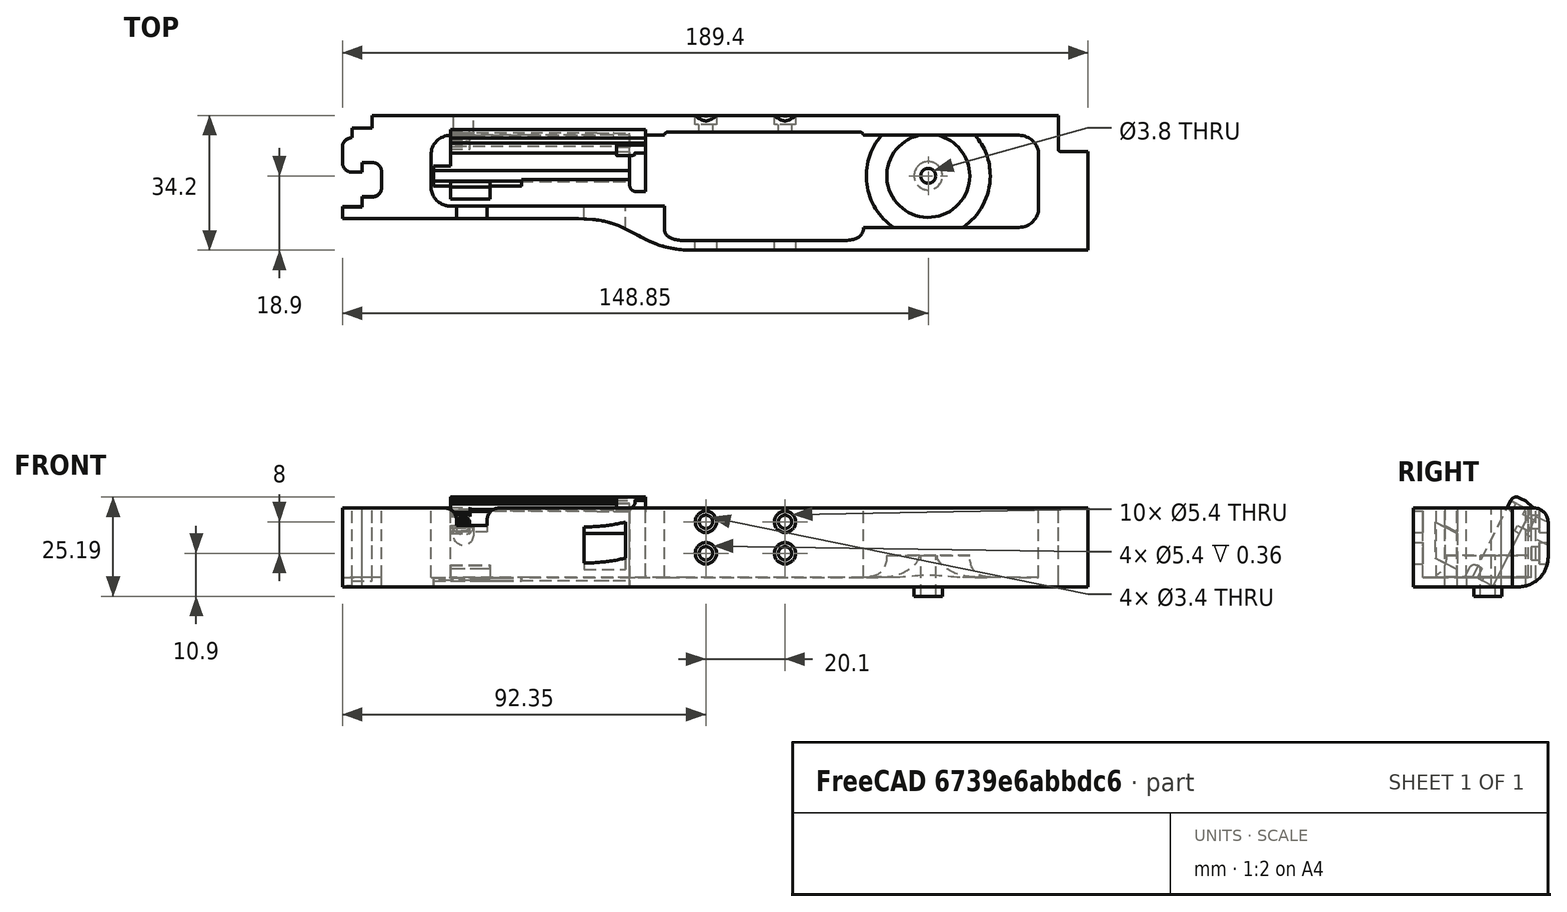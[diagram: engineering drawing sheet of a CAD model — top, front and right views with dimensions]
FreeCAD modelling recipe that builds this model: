
FCSTD DOCUMENT  (FreeCAD 0.19R0.19.2)
Label: v0_993
License: All rights reserved
LicenseURL: http://en.wikipedia.org/wiki/All_rights_reserved
objects: Sketcher::SketchObject×37, Part::Extrusion×31, Part::Cut×14, Part::Fillet×13, Part::MultiFuse×12, Part::Box×8, App::MeasureDistance×4, Part::Revolution×1, Mesh::Feature×1
note: 116 computed .brp shape members not serialized (recipe doc carries the construction recipe); baked Part::Feature solids carry a one-line shape summary decoded from their .brp

FEATURE [Sketcher::SketchObject] Sketch
  FullyConstrained = true
  sketch-geometry (36):
    g0: LineSegment StartX=0 StartY=0 StartZ=0 EndX=154.4 EndY=0 EndZ=0
    g1: LineSegment StartX=154.4 StartY=0 StartZ=0 EndX=154.4 EndY=-7.6 EndZ=0
    g2: LineSegment StartX=32.5209 StartY=-26.2 StartZ=0 EndX=-7.5 EndY=-26.2 EndZ=0
    g3-g7: Circle x5 (B-spline internal-alignment scaffolding for g8; pole/knot coordinates omitted)
    g8: BSplineCurve PolesCount=5 KnotsCount=3 Degree=3 IsPeriodic=0
    g9: GeomPoint X=61.85 Y=-33.8 Z=0
    g10: GeomPoint X=47.185 Y=-29.9 Z=0
    g11: GeomPoint X=32.5209 Y=-26.2 Z=0
    g12: Circle CenterX=121.35 CenterY=-14.3 CenterZ=0 NormalX=0 NormalY=0 NormalZ=1 AngleXU=0 Radius=3.25
    g13: LineSegment StartX=-7.5 StartY=-26.2 StartZ=0 EndX=-27.5 EndY=-26.2 EndZ=0
    g14: LineSegment StartX=-20 StartY=0 StartZ=0 EndX=0 EndY=0 EndZ=0
    g15: LineSegment StartX=-25 StartY=-3.1 StartZ=0 EndX=-20 EndY=-3.1 EndZ=0
    g16: LineSegment StartX=-25 StartY=-3.1 StartZ=0 EndX=-25 EndY=-5.6 EndZ=0
    g17: LineSegment StartX=-27.5 StartY=-8.1 StartZ=0 EndX=-27.5 EndY=-11.85 EndZ=0
    g18: ArcOfCircle CenterX=-25 CenterY=-8.1 CenterZ=0 NormalX=0 NormalY=0 NormalZ=1 AngleXU=0 Radius=2.5 StartAngle=1.5708 EndAngle=3.14159
    g19: LineSegment StartX=-25 StartY=-14.35 StartZ=0 EndX=-22.5 EndY=-14.35 EndZ=0
    g20: ArcOfCircle CenterX=-25 CenterY=-11.85 CenterZ=0 NormalX=0 NormalY=0 NormalZ=1 AngleXU=0 Radius=2.5 StartAngle=3.14159 EndAngle=4.71239
    g21: LineSegment StartX=-22.5 StartY=-14.35 StartZ=0 EndX=-22.5 EndY=-11.85 EndZ=0
    g22: LineSegment StartX=-22.5 StartY=-11.85 StartZ=0 EndX=-20 EndY=-11.85 EndZ=0
    g23: ArcOfCircle CenterX=-20 CenterY=-14.35 CenterZ=0 NormalX=0 NormalY=0 NormalZ=1 AngleXU=0 Radius=2.5 StartAngle=8e-16 EndAngle=1.5708
    g24: LineSegment StartX=-17.5 StartY=-14.35 StartZ=0 EndX=-17.5 EndY=-18.1 EndZ=0
    g25: ArcOfCircle CenterX=-20 CenterY=-18.1 CenterZ=0 NormalX=0 NormalY=0 NormalZ=1 AngleXU=0 Radius=2.5 StartAngle=4.71239 EndAngle=6.28319
    g26: LineSegment StartX=-22.5 StartY=-20.6 StartZ=0 EndX=-20 EndY=-20.6 EndZ=0
    g27: LineSegment StartX=-22.5 StartY=-20.6 StartZ=0 EndX=-22.5 EndY=-23.1 EndZ=0
    g28: LineSegment StartX=-27.5 StartY=-23.1 StartZ=0 EndX=-22.5 EndY=-23.1 EndZ=0
    g29: LineSegment StartX=-20 StartY=-3.1 StartZ=0 EndX=-20 EndY=0 EndZ=0
    g30: LineSegment StartX=-27.5 StartY=-23.1 StartZ=0 EndX=-27.5 EndY=-26.2 EndZ=0
    g31: LineSegment StartX=154.4 StartY=-7.6 StartZ=0 EndX=154.4 EndY=-8.6 EndZ=0
    g32: ArcOfCircle CenterX=154.9 CenterY=-8.6 CenterZ=0 NormalX=0 NormalY=0 NormalZ=1 AngleXU=0 Radius=0.5 StartAngle=3.14159 EndAngle=4.71239
    g33: LineSegment StartX=154.9 StartY=-9.1 StartZ=0 EndX=161.9 EndY=-9.1 EndZ=0
    g34: LineSegment StartX=161.9 StartY=-9.1 StartZ=0 EndX=161.9 EndY=-33.8 EndZ=0
    g35: LineSegment StartX=161.9 StartY=-33.8 StartZ=0 EndX=61.85 EndY=-33.8 EndZ=0
  constraints (72):
    c: PointOnObject(g0,g-2)
    c: Horizontal(g0)
    c: Distance(g0) = 154.4
    c: DistanceY(g-1,g0) = 0
    c: Vertical(g1)
    c: Distance(g1) = 7.6
    c: Coincident(g1,g0)
    c: Horizontal(g2)
    c: Block(g2)
    c: Weight(g3) = 1
    c: Coincident(g8,g2)
    c: InternalAlignment(g3-g7 -> g8) x5
    c: InternalAlignment(g9,g8)
    c: InternalAlignment(g10,g8)
    c: InternalAlignment(g11,g8)
    c: Block(g12)
    c: Coincident(g13,g2)
    c: Horizontal(g13)
    c: Distance(g13) = 20
    c: Horizontal(g14)
    c: Distance(g14) = 20
    c: Coincident(g14,g0)
    c: Horizontal(g15)
    c: Vertical(g16)
    c: Coincident(g16,g15)
    c: Vertical(g17)
    c: Coincident(g18,g16)
    c: Block(g18)
    c: Coincident(g17,g18)
    c: Horizontal(g19)
    c: Coincident(g20,g17)
    c: Block(g20)
    c: Block(g19)
    c: Vertical(g21)
    c: Coincident(g21,g19)
    c: Horizontal(g22)
    c: Coincident(g22,g21)
    c: Coincident(g23,g22)
    c: Vertical(g24)
    c: Block(g23)
    c: Coincident(g24,g23)
    c: Coincident(g25,g24)
    c: Block(g25)
    c: Horizontal(g26)
    c: Coincident(g26,g25)
    c: Vertical(g27)
    c: Coincident(g27,g26)
    c: Horizontal(g28)
    c: Coincident(g28,g27)
    c: Block(g15)
    c: Block(g28)
    c: Coincident(g29,g15)
    c: Coincident(g29,g14)
    c: Vertical(g29)
    c: Coincident(g30,g28)
    c: Coincident(g30,g13)
    c: Vertical(g30)
    c: Vertical(g31)
    c: Distance(g31) = 1
    c: Coincident(g31,g1)
    c: Coincident(g32,g31)
    c: Block(g32)
    c: Coincident(g33,g32)
    c: Horizontal(g33)
    c: Coincident(g34,g33)
    c: Vertical(g34)
    c: Block(g34)
    c: Coincident(g35,g34)
    c: Horizontal(g35)
    c: Block(g35)
    c: Coincident(g8,g35)
    c: Block(g8)
FEATURE [Part::Extrusion] Extrude  label="mainBodyBaseExtrude"
  Base = -> Sketch
  Dir = (0,0,1)
  DirMode = 2
  FaceMakerClass = Part::FaceMakerBullseye
  LengthFwd = 2.4
  LengthRev = 0
  Solid = true
  Symmetric = false
FEATURE [Sketcher::SketchObject] Sketch001
  FullyConstrained = true
  sketch-geometry (75):
    g0: ArcOfCircle CenterX=144.4 CenterY=-10 CenterZ=0 NormalX=0 NormalY=0 NormalZ=1 AngleXU=0 Radius=5 StartAngle=4.345e-13 EndAngle=1.5708
    g1: LineSegment StartX=32.5209 StartY=-26.2 StartZ=0 EndX=-7.49911 EndY=-26.2 EndZ=0
    g2: LineSegment StartX=0 StartY=0 StartZ=0 EndX=154.4 EndY=0 EndZ=0
    g3-g7: Circle x5 (B-spline internal-alignment scaffolding for g8; pole/knot coordinates omitted)
    g8: BSplineCurve PolesCount=5 KnotsCount=3 Degree=3 IsPeriodic=0
    g9: GeomPoint X=61.85 Y=-33.8 Z=0
    g10: GeomPoint X=47.1857 Y=-29.9 Z=0
    g11: GeomPoint X=32.5209 Y=-26.2 Z=0
    g12: LineSegment StartX=154.4 StartY=0 StartZ=0 EndX=154.4 EndY=-7.6 EndZ=0
    g13: LineSegment StartX=20 StartY=-5 StartZ=0 EndX=54.35 EndY=-5 EndZ=0
    g14: LineSegment StartX=104.85 StartY=-5 StartZ=0 EndX=144.4 EndY=-5 EndZ=0
    g15: LineSegment StartX=54.35 StartY=-23 StartZ=0 EndX=20 EndY=-23 EndZ=0
    g16: LineSegment StartX=-27.4991 StartY=-26.2 StartZ=0 EndX=-7.49911 EndY=-26.2 EndZ=0
    g17: LineSegment StartX=-20 StartY=0 StartZ=0 EndX=0 EndY=0 EndZ=0
    g18: LineSegment StartX=-27.4991 StartY=-23.2 StartZ=0 EndX=-22.5 EndY=-23.2 EndZ=0
    g19: LineSegment StartX=-22.5 StartY=-20.7 StartZ=0 EndX=-22.5 EndY=-23.2 EndZ=0
    g20: LineSegment StartX=-22.5 StartY=-20.7 StartZ=0 EndX=-20 EndY=-20.7 EndZ=0
    g21: ArcOfCircle CenterX=-20 CenterY=-18.2 CenterZ=0 NormalX=0 NormalY=0 NormalZ=1 AngleXU=0 Radius=2.5 StartAngle=4.71239 EndAngle=6.28319
    g22: LineSegment StartX=-17.5 StartY=-14.4 StartZ=0 EndX=-17.5 EndY=-18.2 EndZ=0
    g23: ArcOfCircle CenterX=-20 CenterY=-14.4 CenterZ=0 NormalX=0 NormalY=0 NormalZ=1 AngleXU=0 Radius=2.5 StartAngle=9e-16 EndAngle=1.5708
    g24: LineSegment StartX=-22.5 StartY=-11.9 StartZ=0 EndX=-20 EndY=-11.9 EndZ=0
    g25: LineSegment StartX=-22.5 StartY=-14.4 StartZ=0 EndX=-22.5 EndY=-11.9 EndZ=0
    g26: LineSegment StartX=-25 StartY=-14.4 StartZ=0 EndX=-22.5 EndY=-14.4 EndZ=0
    g27: ArcOfCircle CenterX=-25 CenterY=-11.9 CenterZ=0 NormalX=0 NormalY=0 NormalZ=1 AngleXU=0 Radius=2.5 StartAngle=3.14159 EndAngle=4.71239
    g28: LineSegment StartX=-27.5 StartY=-8.1 StartZ=0 EndX=-27.5 EndY=-11.9 EndZ=0
    g29: ArcOfCircle CenterX=-25 CenterY=-8.1 CenterZ=0 NormalX=0 NormalY=0 NormalZ=1 AngleXU=0 Radius=2.5 StartAngle=1.5708 EndAngle=3.14159
    g30: LineSegment StartX=-25 StartY=-3.1 StartZ=0 EndX=-25 EndY=-5.6 EndZ=0
    g31: LineSegment StartX=-20 StartY=-3.1 StartZ=0 EndX=-25 EndY=-3.1 EndZ=0
    g32: LineSegment StartX=-20 StartY=0 StartZ=0 EndX=-20 EndY=-3.1 EndZ=0
    g33: LineSegment StartX=-27.4991 StartY=-26.2 StartZ=0 EndX=-27.4991 EndY=-23.2 EndZ=0
    g34: LineSegment StartX=4.09e-14 StartY=-5 StartZ=0 EndX=20 EndY=-5 EndZ=0
    g35: ArcOfCircle CenterX=7.1e-15 CenterY=-18 CenterZ=0 NormalX=0 NormalY=0 NormalZ=1 AngleXU=0 Radius=5 StartAngle=3.14159 EndAngle=4.71239
    g36: ArcOfCircle CenterX=4.26e-14 CenterY=-10 CenterZ=0 NormalX=0 NormalY=0 NormalZ=1 AngleXU=0 Radius=5 StartAngle=1.5708 EndAngle=3.14159
    g37: LineSegment StartX=-5 StartY=-18 StartZ=0 EndX=-5 EndY=-10 EndZ=0
    g38: LineSegment StartX=6.2e-15 StartY=-23 StartZ=0 EndX=20 EndY=-23 EndZ=0
    g39: LineSegment StartX=154.4 StartY=-7.6 StartZ=0 EndX=154.4 EndY=-8.6 EndZ=0
    g40: LineSegment StartX=154.9 StartY=-9.1 StartZ=0 EndX=161.9 EndY=-9.1 EndZ=0
    g41: ArcOfCircle CenterX=154.9 CenterY=-8.6 CenterZ=0 NormalX=0 NormalY=0 NormalZ=1 AngleXU=0 Radius=0.5 StartAngle=3.14159 EndAngle=4.71299
    g42: LineSegment StartX=104.85 StartY=-28.3916 StartZ=0 EndX=144.408 EndY=-28.3916 EndZ=0
    g43: LineSegment StartX=149.4 StartY=-10 StartZ=0 EndX=149.4 EndY=-23.4 EndZ=0
    g44: ArcOfCircle CenterX=144.408 CenterY=-23.4 CenterZ=0 NormalX=0 NormalY=0 NormalZ=1 AngleXU=0 Radius=4.99164 StartAngle=4.71239 EndAngle=6.28319
    g45: LineSegment StartX=104.85 StartY=-28.3916 StartZ=0 EndX=104.85 EndY=-28.7833 EndZ=0
    g46: LineSegment StartX=54.35 StartY=-28.7916 StartZ=0 EndX=54.35 EndY=-23 EndZ=0
    g47: LineSegment StartX=161.9 StartY=-33.8 StartZ=0 EndX=161.9 EndY=-9.1 EndZ=0
    g48: LineSegment StartX=61.85 StartY=-33.8 StartZ=0 EndX=161.9 EndY=-33.8 EndZ=0
    g49: Circle CenterX=54.35 CenterY=-28.7916 CenterZ=0 NormalX=0 NormalY=0 NormalZ=1 AngleXU=0 Radius=1
    g50: Circle CenterX=54.35 CenterY=-31.7916 CenterZ=0 NormalX=0 NormalY=0 NormalZ=1 AngleXU=0 Radius=1
    g51: Circle CenterX=57.35 CenterY=-31.7916 CenterZ=0 NormalX=0 NormalY=0 NormalZ=1 AngleXU=0 Radius=1
    g52: BSplineCurve PolesCount=3 KnotsCount=2 Degree=2 IsPeriodic=0
    g53: GeomPoint X=54.35 Y=-28.7916 Z=0
    g54: GeomPoint X=57.35 Y=-31.7916 Z=0
    g55: Circle CenterX=104.85 CenterY=-28.7833 CenterZ=0 NormalX=0 NormalY=0 NormalZ=1 AngleXU=0 Radius=1
    g56: Circle CenterX=104.85 CenterY=-31.7916 CenterZ=0 NormalX=0 NormalY=0 NormalZ=1 AngleXU=0 Radius=1
    g57: Circle CenterX=101.85 CenterY=-31.7916 CenterZ=0 NormalX=0 NormalY=0 NormalZ=1 AngleXU=0 Radius=1
    g58: BSplineCurve PolesCount=3 KnotsCount=2 Degree=2 IsPeriodic=0
    g59: GeomPoint X=104.85 Y=-28.7833 Z=0
    g60: GeomPoint X=101.85 Y=-31.7916 Z=0
    g61: LineSegment StartX=57.35 StartY=-31.7916 StartZ=0 EndX=101.85 EndY=-31.7916 EndZ=0
    g62: Circle CenterX=54.35 CenterY=-5 CenterZ=0 NormalX=0 NormalY=0 NormalZ=1 AngleXU=0 Radius=1
    g63: Circle CenterX=54.35 CenterY=-4 CenterZ=0 NormalX=0 NormalY=0 NormalZ=1 AngleXU=0 Radius=1
    g64: Circle CenterX=55.15 CenterY=-4 CenterZ=0 NormalX=0 NormalY=0 NormalZ=1 AngleXU=0 Radius=1
    g65: BSplineCurve PolesCount=3 KnotsCount=2 Degree=2 IsPeriodic=0
    g66: GeomPoint X=54.35 Y=-5 Z=0
    g67: GeomPoint X=55.15 Y=-4 Z=0
    g68: Circle CenterX=104.85 CenterY=-5 CenterZ=0 NormalX=0 NormalY=0 NormalZ=1 AngleXU=0 Radius=1
    g69: Circle CenterX=104.85 CenterY=-4 CenterZ=0 NormalX=0 NormalY=0 NormalZ=1 AngleXU=0 Radius=1
    g70: Circle CenterX=104.05 CenterY=-4 CenterZ=0 NormalX=0 NormalY=0 NormalZ=1 AngleXU=0 Radius=1
    g71: BSplineCurve PolesCount=3 KnotsCount=2 Degree=2 IsPeriodic=0
    g72: GeomPoint X=104.85 Y=-5 Z=0
    g73: GeomPoint X=104.05 Y=-4 Z=0
    g74: LineSegment StartX=104.05 StartY=-4 StartZ=0 EndX=55.15 EndY=-4 EndZ=0
  constraints (156):
    c: PointOnObject(g2,g-2)
    c: DistanceY(g-1,g2) = 0
    c: Block(g0)
    c: Horizontal(g1)
    c: Distance(g1) = 40.02
    c: Horizontal(g2)
    c: Block(g2)
    c: Weight(g3) = 1
    c: Equal(g3, g4-g7) x4
    c: Coincident(g8,g1)
    c: InternalAlignment(g3-g7 -> g8) x5
    c: InternalAlignment(g9,g8)
    c: InternalAlignment(g10,g8)
    c: InternalAlignment(g11,g8)
    c: Vertical(g12)
    c: Coincident(g12,g2)
    c: Distance(g12) = 7.6
    c: Block(g12)
    c: Horizontal(g13)
    c: Coincident(g14,g0)
    c: Horizontal(g14)
    c: Horizontal(g15)
    c: Horizontal(g16)
    c: Distance(g16) = 20
    c: Coincident(g1,g16)
    c: Horizontal(g17)
    c: Distance(g17) = 20
    c: Coincident(g17,g2)
    c: Horizontal(g31)
    c: Vertical(g30)
    c: Coincident(g29,g30)
    c: Vertical(g28)
    c: Block(g29)
    c: Coincident(g27,g28)
    c: Block(g27)
    c: Horizontal(g26)
    c: Coincident(g26,g27)
    c: Vertical(g25)
    c: Coincident(g25,g26)
    c: Horizontal(g24)
    c: Coincident(g23,g24)
    c: Block(g23)
    c: Vertical(g22)
    c: Coincident(g21,g22)
    c: Block(g21)
    c: Horizontal(g20)
    c: Coincident(g20,g21)
    c: Vertical(g19)
    c: Coincident(g19,g20)
    c: Horizontal(g18)
    c: Coincident(g18,g19)
    c: Coincident(g32,g17)
    c: Coincident(g32,g31)
    c: Vertical(g32)
    c: Coincident(g33,g16)
    c: Coincident(g33,g18)
    c: Vertical(g33)
    c: Block(g33)
    c: Block(g18)
    c: Block(g22)
    c: Block(g26)
    c: Block(g25)
    c: Block(g24)
    c: Block(g28)
    c: Block(g31)
    c: Block(g30)
    c: Horizontal(g34)
    c: Distance(g34) = 20
    c: Block(g35)
    c: Block(g36)
    c: Coincident(g37,g35)
    c: Coincident(g37,g36)
    c: Vertical(g37)
    c: Coincident(g38,g35)
    c: Coincident(g38,g15)
    c: Horizontal(g38)
    c: Block(g38)
    c: Block(g34)
    c: Block(g13)
    c: Vertical(g39)
    c: Distance(g39) = 1
    c: Coincident(g39,g12)
    c: Horizontal(g40)
    c: Coincident(g41,g39)
    c: Coincident(g41,g40)
    c: Block(g39)
    c: Block(g41)
    c: Horizontal(g42)
    c: Vertical(g43)
    c: Distance(g43) = 13.4
    c: Coincident(g43,g0)
    c: Block(g42)
    c: Block(g43)
    c: Coincident(g44,g43)
    c: Coincident(g44,g42)
    c: Block(g44)
    c: Distance(g15) = 34.35
    c: Coincident(g45,g42)
    c: Vertical(g45)
    c: Coincident(g46,g15)
    c: Vertical(g46)
    c: Coincident(g47,g40)
    c: Vertical(g47)
    c: Block(g47)
    c: Coincident(g48,g47)
    c: Horizontal(g48)
    c: Block(g48)
    c: Coincident(g8,g48)
    c: Block(g8)
    c: Coincident(g52,g46)
    c: Weight(g49) = 1
    c: Equal(g49,g50)
    c: Equal(g49,g51)
    c: InternalAlignment(g49,g52)
    c: InternalAlignment(g50,g52)
    c: InternalAlignment(g51,g52)
    c: InternalAlignment(g53,g52)
    c: InternalAlignment(g54,g52)
    c: Coincident(g58,g45)
    c: Weight(g55) = 1
    c: Equal(g55,g56)
    c: Equal(g55,g57)
    c: InternalAlignment(g55,g58)
    c: InternalAlignment(g56,g58)
    c: InternalAlignment(g57,g58)
    c: InternalAlignment(g59,g58)
    c: InternalAlignment(g60,g58)
    c: Block(g58)
    c: Block(g52)
    c: Coincident(g61,g52)
    c: Coincident(g61,g58)
    c: Horizontal(g61)
    c: Block(g14)
    c: Coincident(g65,g13)
    c: Weight(g62) = 1
    c: Equal(g62,g63)
    c: Equal(g62,g64)
    c: InternalAlignment(g62,g65)
    c: InternalAlignment(g63,g65)
    c: InternalAlignment(g64,g65)
    c: InternalAlignment(g66,g65)
    c: InternalAlignment(g67,g65)
    c: Block(g65)
    c: Coincident(g71,g14)
    c: Weight(g68) = 1
    c: Equal(g68,g69)
    c: Equal(g68,g70)
    c: InternalAlignment(g68,g71)
    c: InternalAlignment(g69,g71)
    c: InternalAlignment(g70,g71)
    c: InternalAlignment(g72,g71)
    c: InternalAlignment(g73,g71)
    c: Block(g71)
    c: Coincident(g74,g71)
    c: Coincident(g74,g65)
    c: Horizontal(g74)
FEATURE [Sketcher::SketchObject] Sketch005
  FullyConstrained = true
  Placement = pos=(0,0,0) rot=(1,0,0;1.5708rad)
  sketch-geometry (4):
    g0: Circle CenterX=84.95 CenterY=16.5 CenterZ=0 NormalX=0 NormalY=0 NormalZ=1 AngleXU=0 Radius=1.7
    g1: Circle CenterX=84.95 CenterY=8.5 CenterZ=0 NormalX=0 NormalY=0 NormalZ=1 AngleXU=0 Radius=1.7
    g2: Circle CenterX=64.85 CenterY=8.5 CenterZ=0 NormalX=0 NormalY=0 NormalZ=1 AngleXU=0 Radius=1.7
    g3: Circle CenterX=64.85 CenterY=16.5 CenterZ=0 NormalX=0 NormalY=0 NormalZ=1 AngleXU=0 Radius=1.7
  constraints (4):
    c: Block(g0)
    c: Block(g1)
    c: Block(g2)
    c: Block(g3)
FEATURE [Part::Extrusion] Extrude004  label="removeFromMainBodyToCreateScrewHolesForSolenoidExtrude004"
  Base = -> Sketch005
  Dir = (0,-1,1.1e-15)
  DirMode = 2
  FaceMakerClass = Part::FaceMakerBullseye
  LengthFwd = 10
  LengthRev = 0
  Solid = true
  Symmetric = false
FEATURE [Sketcher::SketchObject] Sketch004
  FullyConstrained = true
  Placement = pos=(0,0,0) rot=(1,0,0;1.5708rad)
  sketch-geometry (12):
    g0: LineSegment StartX=15.75 StartY=2.5 StartZ=0 EndX=15.75 EndY=0 EndZ=0
    g1: Circle CenterX=15.75 CenterY=2.5 CenterZ=0 NormalX=0 NormalY=0 NormalZ=1 AngleXU=0 Radius=1
    g2: Circle CenterX=10.55 CenterY=2.5 CenterZ=0 NormalX=0 NormalY=0 NormalZ=1 AngleXU=0 Radius=1
    g3: Circle CenterX=10.55 CenterY=8 CenterZ=0 NormalX=0 NormalY=0 NormalZ=1 AngleXU=0 Radius=1
    g4: BSplineCurve PolesCount=3 KnotsCount=2 Degree=2 IsPeriodic=0
    g5: GeomPoint X=15.75 Y=2.5 Z=0
    g6: GeomPoint X=10.55 Y=8 Z=0
    g7: LineSegment StartX=1.9 StartY=8 StartZ=0 EndX=10.55 EndY=8 EndZ=0
    g8: LineSegment StartX=1.9 StartY=-2.4 StartZ=0 EndX=1.9 EndY=8 EndZ=0
    g9: LineSegment StartX=3.30092 StartY=-2.4 StartZ=0 EndX=3.30092 EndY=0 EndZ=0
    g10: LineSegment StartX=15.75 StartY=0 StartZ=0 EndX=3.30092 EndY=0 EndZ=0
    g11: LineSegment StartX=3.30092 StartY=-2.4 StartZ=0 EndX=1.9 EndY=-2.4 EndZ=0
  constraints (26):
    c: Vertical(g0)
    c: Distance(g0) = 2.5
    c: Coincident(g4,g0)
    c: Weight(g1) = 1
    c: Equal(g1,g2)
    c: Equal(g1,g3)
    c: InternalAlignment(g1,g4)
    c: InternalAlignment(g2,g4)
    c: InternalAlignment(g3,g4)
    c: InternalAlignment(g5,g4)
    c: InternalAlignment(g6,g4)
    c: Block(g4)
    c: Coincident(g7,g4)
    c: Horizontal(g7)
    c: Vertical(g8)
    c: Coincident(g8,g7)
    c: Block(g8)
    c: Vertical(g9)
    c: Coincident(g10,g0)
    c: PointOnObject(g10,g-1)
    c: Horizontal(g10)
    c: Coincident(g10,g9)
    c: Block(g9)
    c: Coincident(g11,g9)
    c: Coincident(g11,g8)
    c: Horizontal(g11)
FEATURE [Sketcher::SketchObject] Sketch007
  FullyConstrained = true
  Placement = pos=(0,-14.3,2.37) rot=(-1,0,0;2.03453rad)
  sketch-geometry (6):
    g0: LineSegment StartX=0 StartY=0 StartZ=0 EndX=45.5 EndY=0 EndZ=0
    g1: LineSegment StartX=0 StartY=0 StartZ=0 EndX=0 EndY=-21.2 EndZ=0
    g2: LineSegment StartX=45.5 StartY=0 StartZ=0 EndX=49.5 EndY=0 EndZ=0
    g3: LineSegment StartX=49.5 StartY=0 StartZ=0 EndX=49.5 EndY=-21.2 EndZ=0
    g4: LineSegment StartX=49.5 StartY=-21.2 StartZ=0 EndX=0 EndY=-21.2 EndZ=0
    g5: Circle CenterX=3.25 CenterY=-18.05 CenterZ=0 NormalX=0 NormalY=0 NormalZ=1 AngleXU=0 Radius=1.6
  constraints (15):
    c: Coincident(g0,g-1)
    c: Horizontal(g0)
    c: Distance(g0) = 45.5
    c: Coincident(g1,g0)
    c: Vertical(g1)
    c: Horizontal(g2)
    c: Distance(g2) = 4
    c: Coincident(g2,g0)
    c: Coincident(g3,g2)
    c: Vertical(g3)
    c: Block(g3)
    c: Coincident(g4,g3)
    c: Horizontal(g4)
    c: Coincident(g4,g1)
    c: Block(g5)
FEATURE [Part::Extrusion] Extrude005  label="solenoidDriverHolderExtrude005"
  Base = -> Sketch007
  Dir = (0,0.894389,-0.447291)
  DirMode = 2
  FaceMakerClass = Part::FaceMakerBullseye
  LengthFwd = 10
  LengthRev = 0
  Placement = pos=(0,0,-2) rot=(0,0,1;0rad)
  Solid = true
  Symmetric = false
FEATURE [Sketcher::SketchObject] Sketch008
  FullyConstrained = false
  Placement = pos=(0,-4.3,-2.6) rot=(-1,0,0;2.03453rad)
  sketch-geometry (1):
    g0: Circle CenterX=42.25 CenterY=-3.15 CenterZ=0 NormalX=0 NormalY=0 NormalZ=1 AngleXU=0 Radius=4.5
FEATURE [Sketcher::SketchObject] Sketch009
  FullyConstrained = true
  Placement = pos=(0,-4.3,-2.6) rot=(-1,0,0;2.03453rad)
  sketch-geometry (1):
    g0: Circle CenterX=3.25 CenterY=-18.0217 CenterZ=0 NormalX=0 NormalY=0 NormalZ=1 AngleXU=0 Radius=2.8
  constraints (1):
    c: Block(g0)
FEATURE [Sketcher::SketchObject] Sketch010
  FullyConstrained = true
  Placement = pos=(0,-14.3,2.37) rot=(-1,0,0;2.03453rad)
  sketch-geometry (1):
    g0: Circle CenterX=3.25 CenterY=-18.05 CenterZ=0 NormalX=0 NormalY=0 NormalZ=1 AngleXU=0 Radius=1.6
  constraints (1):
    c: Block(g0)
FEATURE [Part::Extrusion] Extrude008  label="removeFromScrewHole3"
  Base = -> Sketch010
  Dir = (0,0.894389,-0.447291)
  DirMode = 2
  FaceMakerClass = Part::FaceMakerBullseye
  LengthFwd = -25
  LengthRev = 0
  Placement = pos=(0,4,-4) rot=(0,0,1;0rad)
  Solid = true
  Symmetric = false
FEATURE [Sketcher::SketchObject] Sketch011
  FullyConstrained = true
  Placement = pos=(0,-14.3,2.37) rot=(-1,0,0;2.03453rad)
  sketch-geometry (4):
    g0: LineSegment StartX=49.5 StartY=-21.2 StartZ=0 EndX=49.5 EndY=-22.8 EndZ=0
    g1: LineSegment StartX=49.5 StartY=-22.8 StartZ=0 EndX=0.002238 EndY=-22.8 EndZ=0
    g2: LineSegment StartX=0.002238 StartY=-21.2 StartZ=0 EndX=0.002238 EndY=-22.8 EndZ=0
    g3: LineSegment StartX=49.5 StartY=-21.2 StartZ=0 EndX=0.002238 EndY=-21.2 EndZ=0
  constraints (10):
    c: Vertical(g0)
    c: Distance(g0) = 1.6
    c: Coincident(g1,g0)
    c: Horizontal(g1)
    c: Vertical(g2)
    c: Coincident(g2,g1)
    c: Coincident(g3,g0)
    c: Coincident(g3,g2)
    c: Horizontal(g3)
    c: Block(g3)
FEATURE [Part::Extrusion] Extrude009  label="solenoidDriverTopLipFront"
  Base = -> Sketch011
  Dir = (0,0.894389,-0.447291)
  DirMode = 2
  FaceMakerClass = Part::FaceMakerBullseye
  LengthFwd = -2
  LengthRev = 0
  Placement = pos=(0,-2.9,-0.35) rot=(0,0,1;0rad)
  Solid = true
  Symmetric = false
FEATURE [Sketcher::SketchObject] Sketch012
  FullyConstrained = true
  Placement = pos=(0,-14.3,2.37) rot=(-1,0,0;2.03453rad)
  sketch-geometry (4):
    g0: LineSegment StartX=49.5 StartY=-21.2 StartZ=0 EndX=49.5 EndY=-22.8 EndZ=0
    g1: LineSegment StartX=49.5 StartY=-22.8 StartZ=0 EndX=0.002238 EndY=-22.8 EndZ=0
    g2: LineSegment StartX=0.002238 StartY=-21.2 StartZ=0 EndX=0.002238 EndY=-22.8 EndZ=0
    g3: LineSegment StartX=49.5 StartY=-21.2 StartZ=0 EndX=0.002238 EndY=-21.2 EndZ=0
  constraints (10):
    c: Vertical(g0)
    c: Distance(g0) = 1.6
    c: Coincident(g1,g0)
    c: Horizontal(g1)
    c: Vertical(g2)
    c: Coincident(g2,g1)
    c: Coincident(g3,g0)
    c: Coincident(g3,g2)
    c: Horizontal(g3)
    c: Block(g3)
FEATURE [Part::Extrusion] Extrude010  label="solenoidDriverTopLipLowerExtrude010"
  Base = -> Sketch012
  Dir = (0,0.894389,-0.447291)
  DirMode = 2
  FaceMakerClass = Part::FaceMakerBullseye
  LengthFwd = 5.05
  LengthRev = 0
  Solid = true
  Symmetric = false
FEATURE [Sketcher::SketchObject] Sketch015
  FullyConstrained = true
  Placement = pos=(0,-14.3,2.37) rot=(-1,0,0;2.03453rad)
  sketch-geometry (4):
    g0: LineSegment StartX=0 StartY=1.5 StartZ=0 EndX=0 EndY=0 EndZ=0
    g1: LineSegment StartX=0 StartY=1.5 StartZ=0 EndX=5 EndY=1.5 EndZ=0
    g2: LineSegment StartX=5 StartY=1.5 StartZ=0 EndX=5 EndY=0 EndZ=0
    g3: LineSegment StartX=0 StartY=0 StartZ=0 EndX=5 EndY=0 EndZ=0
  constraints (13):
    c: Vertical(g0)
    c: Distance(g0) = 1.5
    c: Horizontal(g1)
    c: Distance(g1) = 5
    c: Coincident(g1,g0)
    c: Vertical(g2)
    c: Distance(g2) = 1.5
    c: Coincident(g2,g1)
    c: Block(g1)
    c: Block(g2)
    c: Block(g0)
    c: Coincident(g3,g0)
    c: Coincident(g3,g2)
FEATURE [Part::Extrusion] Extrude013  label="solenoidDriverBottomLipTopExtrude012"
  Base = -> Sketch015
  Dir = (0,0.894389,-0.447291)
  DirMode = 2
  FaceMakerClass = Part::FaceMakerBullseye
  LengthFwd = -6.5
  LengthRev = 0
  Placement = pos=(0,-14.15,19.65) rot=(1,0,0;1.5708rad)
  Solid = true
  Symmetric = false
FEATURE [Sketcher::SketchObject] Sketch016
  FullyConstrained = true
  Placement = pos=(0,0,0) rot=(1,0,0;1.5708rad)
  sketch-geometry (4):
    g0: Circle CenterX=84.15 CenterY=16.5 CenterZ=0 NormalX=0 NormalY=0 NormalZ=1 AngleXU=0 Radius=2.7
    g1: Circle CenterX=64.05 CenterY=16.5 CenterZ=0 NormalX=0 NormalY=0 NormalZ=1 AngleXU=0 Radius=2.7
    g2: Circle CenterX=64.05 CenterY=8.5 CenterZ=0 NormalX=0 NormalY=0 NormalZ=1 AngleXU=0 Radius=2.7
    g3: Circle CenterX=84.15 CenterY=8.5 CenterZ=0 NormalX=0 NormalY=0 NormalZ=1 AngleXU=0 Radius=2.7
  constraints (4):
    c: Block(g0)
    c: Block(g1)
    c: Block(g3)
    c: Block(g2)
FEATURE [Part::Extrusion] Extrude014  label="removeFromMainBodyToCreateScrewHoleCounterSinks"
  Base = -> Sketch016
  Dir = (0,-1,1.1e-15)
  DirMode = 2
  FaceMakerClass = Part::FaceMakerBullseye
  LengthFwd = 1.9
  LengthRev = 0
  Placement = pos=(0.8,-0.36,0) rot=(0,0,1;0rad)
  Solid = true
  Symmetric = false
FEATURE [Part::Extrusion] Extrude015  label="removeFromScrewHole2Extrude007"
  Base = -> Sketch009
  Dir = (0,0.894389,-0.447291)
  DirMode = 2
  FaceMakerClass = Part::FaceMakerBullseye
  LengthFwd = 10
  LengthRev = 0
  Placement = pos=(0,-8,2) rot=(0,0,1;0rad)
  Solid = true
  Symmetric = false
FEATURE [Sketcher::SketchObject] Sketch017
  FullyConstrained = true
  Placement = pos=(0,-14.3,2.37) rot=(-1,0,0;2.03453rad)
  sketch-geometry (4):
    g0: LineSegment StartX=0 StartY=1.5 StartZ=0 EndX=0 EndY=0 EndZ=0
    g1: LineSegment StartX=0 StartY=1.5 StartZ=0 EndX=5 EndY=1.5 EndZ=0
    g2: LineSegment StartX=5 StartY=1.5 StartZ=0 EndX=5 EndY=0 EndZ=0
    g3: LineSegment StartX=0 StartY=0 StartZ=0 EndX=5 EndY=0 EndZ=0
  constraints (13):
    c: Vertical(g0)
    c: Distance(g0) = 1.5
    c: Horizontal(g1)
    c: Distance(g1) = 5
    c: Coincident(g1,g0)
    c: Vertical(g2)
    c: Distance(g2) = 1.5
    c: Coincident(g2,g1)
    c: Block(g1)
    c: Block(g2)
    c: Block(g0)
    c: Coincident(g3,g0)
    c: Coincident(g3,g2)
FEATURE [Part::Extrusion] Extrude016  label="solenoidDriverBottomLipTopExtrude013"
  Base = -> Sketch017
  Dir = (0,0.894389,-0.447291)
  DirMode = 2
  FaceMakerClass = Part::FaceMakerBullseye
  LengthFwd = -6.5
  LengthRev = 0
  Placement = pos=(0,-15.45,20.3) rot=(1,0,0;1.5708rad)
  Solid = true
  Symmetric = false
FEATURE [Part::Fillet] Fillet005  label="solenoidDriverBottomLipTopFillet005"
  Base = -> Extrude016
  Edges = 1 edges r=1.4: [Edge6]
FEATURE [Sketcher::SketchObject] Sketch018
  FullyConstrained = true
  Placement = pos=(38.5,-14.3,2.37) rot=(-1,0,0;2.03453rad)
  sketch-geometry (4):
    g0: LineSegment StartX=11 StartY=0 StartZ=0 EndX=11 EndY=1.5 EndZ=0
    g1: LineSegment StartX=11 StartY=0 StartZ=0 EndX=3.6 EndY=0 EndZ=0
    g2: LineSegment StartX=3.6 StartY=0 StartZ=0 EndX=3.6 EndY=1.5 EndZ=0
    g3: LineSegment StartX=11 StartY=1.5 StartZ=0 EndX=3.6 EndY=1.5 EndZ=0
  constraints (12):
    c: PointOnObject(g0,g-1)
    c: Vertical(g0)
    c: Distance(g0) = 1.5
    c: Horizontal(g1)
    c: Distance(g1) = 7.4
    c: Coincident(g1,g0)
    c: Block(g0)
    c: Coincident(g2,g1)
    c: Vertical(g2)
    c: Coincident(g3,g0)
    c: Horizontal(g3)
    c: Coincident(g2,g3)
FEATURE [Part::Extrusion] Extrude017
  Base = -> Sketch018
  Dir = (0,0.894389,-0.447291)
  DirMode = 2
  FaceMakerClass = Part::FaceMakerBullseye
  LengthFwd = 4
  LengthRev = 0
  Placement = pos=(0,-8.212,34.025) rot=(1,0,0;1.5708rad)
  Solid = true
  Symmetric = false
FEATURE [Sketcher::SketchObject] Sketch019
  FullyConstrained = true
  Placement = pos=(0,0,0) rot=(1,0,0;1.5708rad)
  sketch-geometry (4):
    g0: Circle CenterX=84.95 CenterY=8.5 CenterZ=0 NormalX=0 NormalY=0 NormalZ=1 AngleXU=0 Radius=2.7
    g1: Circle CenterX=64.85 CenterY=8.5 CenterZ=0 NormalX=0 NormalY=0 NormalZ=1 AngleXU=0 Radius=2.7
    g2: Circle CenterX=64.85 CenterY=16.5 CenterZ=0 NormalX=0 NormalY=0 NormalZ=1 AngleXU=0 Radius=2.7
    g3: Circle CenterX=84.95 CenterY=16.5 CenterZ=0 NormalX=0 NormalY=0 NormalZ=1 AngleXU=0 Radius=2.7
  constraints (4):
    c: Block(g3)
    c: Block(g2)
    c: Block(g0)
    c: Block(g1)
FEATURE [Part::Extrusion] Extrude019  label="removeSolenoidAdjusterHoles"
  Base = -> Sketch019
  Dir = (0,-1,1.1e-15)
  DirMode = 2
  FaceMakerClass = Part::FaceMakerBullseye
  LengthFwd = 6
  LengthRev = 0
  Placement = pos=(0,-30,0) rot=(0,0,1;0rad)
  Solid = true
  Symmetric = false
FEATURE [Sketcher::SketchObject] Sketch020
  FullyConstrained = true
  Placement = pos=(0,-14.3,2.37) rot=(-1,0,0;2.03453rad)
  sketch-geometry (6):
    g0: LineSegment StartX=45.5 StartY=-21.2 StartZ=0 EndX=49.5 EndY=-21.2 EndZ=0
    g1: LineSegment StartX=45.5 StartY=0 StartZ=0 EndX=49.5 EndY=0 EndZ=0
    g2: LineSegment StartX=49.5 StartY=0 StartZ=0 EndX=49.5 EndY=-21.2 EndZ=0
    g3: LineSegment StartX=4 StartY=0 StartZ=0 EndX=4 EndY=-21.2 EndZ=0
    g4: LineSegment StartX=45.5 StartY=-21.2 StartZ=0 EndX=4 EndY=-21.2 EndZ=0
    g5: LineSegment StartX=4 StartY=0 StartZ=0 EndX=45.5 EndY=0 EndZ=0
  constraints (16):
    c: Horizontal(g0)
    c: Distance(g0) = 4
    c: Horizontal(g1)
    c: Distance(g1) = 4
    c: Coincident(g2,g1)
    c: Coincident(g2,g0)
    c: Vertical(g2)
    c: Block(g2)
    c: Vertical(g3)
    c: Coincident(g4,g0)
    c: Horizontal(g4)
    c: Coincident(g4,g3)
    c: Coincident(g5,g1)
    c: Horizontal(g5)
    c: Block(g3)
    c: Block(g5)
FEATURE [Part::Box] Box  label="Cube"
  AttacherType = Attacher::AttachEngine3D
  Height = 10
  Length = 190
  Placement = pos=(-30,0,0) rot=(0,0,1;0rad)
  Width = 10
FEATURE [Part::Fillet] Fillet008
  Base = -> Box
  Edges = 1 edges r=7.5: [Edge11]
FEATURE [Part::Box] Box001  label="Cube001"
  AttacherType = Attacher::AttachEngine3D
  Height = 10
  Length = 190
  Placement = pos=(-35,0,0) rot=(0,0,1;0rad)
  Width = 10
FEATURE [Part::Cut] Cut  label="filletMain"
  Base = -> Box001
  Placement = pos=(0,-10,0) rot=(0,0,1;0rad)
  Tool = -> Fillet008
FEATURE [Part::Box] Box002  label="Cube002"
  AttacherType = Attacher::AttachEngine3D
  Height = 30
  Length = 190
  Placement = pos=(-20,0,0) rot=(0,0,1;0rad)
  Width = 10
FEATURE [Part::Box] Box003  label="Cube003"
  AttacherType = Attacher::AttachEngine3D
  Height = 10
  Length = 190
  Placement = pos=(-90,-50,-10) rot=(0,0,1;0rad)
  Width = 50
FEATURE [Sketcher::SketchObject] Sketch021
  FullyConstrained = true
  Placement = pos=(0,-14.3,2.37) rot=(-1,0,0;2.03453rad)
  sketch-geometry (6):
    g0: LineSegment StartX=41.65 StartY=-3.15 StartZ=0 EndX=38.95 EndY=-3.15 EndZ=0
    g1: LineSegment StartX=36.25 StartY=-3.15 StartZ=0 EndX=38.95 EndY=-3.15 EndZ=0
    g2: LineSegment StartX=41.65 StartY=-3.15 StartZ=0 EndX=41.65 EndY=-7.15 EndZ=0
    g3: LineSegment StartX=38.95 StartY=-7.15 StartZ=0 EndX=41.65 EndY=-7.15 EndZ=0
    g4: LineSegment StartX=38.95 StartY=-7.15 StartZ=0 EndX=36.25 EndY=-7.15 EndZ=0
    g5: LineSegment StartX=36.25 StartY=-3.15 StartZ=0 EndX=36.25 EndY=-7.15 EndZ=0
  constraints (16):
    c: Horizontal(g0)
    c: Distance(g0) = 2.7
    c: Horizontal(g1)
    c: Distance(g1) = 2.7
    c: Coincident(g1,g0)
    c: Block(g0)
    c: Coincident(g2,g0)
    c: Vertical(g2)
    c: Horizontal(g3)
    c: Coincident(g3,g2)
    c: Horizontal(g4)
    c: Coincident(g5,g1)
    c: Vertical(g5)
    c: Coincident(g5,g4)
    c: Block(g3)
    c: Block(g4)
FEATURE [Sketcher::SketchObject] Sketch022
  FullyConstrained = true
  Placement = pos=(0,-14.3,2.37) rot=(-1,0,0;2.03453rad)
  sketch-geometry (6):
    g0: LineSegment StartX=41.65 StartY=-3.15 StartZ=0 EndX=38.95 EndY=-3.15 EndZ=0
    g1: LineSegment StartX=36.25 StartY=-3.15 StartZ=0 EndX=38.95 EndY=-3.15 EndZ=0
    g2: LineSegment StartX=41.65 StartY=-3.15 StartZ=0 EndX=41.65 EndY=-7.15 EndZ=0
    g3: LineSegment StartX=38.95 StartY=-7.15 StartZ=0 EndX=41.65 EndY=-7.15 EndZ=0
    g4: LineSegment StartX=38.95 StartY=-7.15 StartZ=0 EndX=36.25 EndY=-7.15 EndZ=0
    g5: LineSegment StartX=36.25 StartY=-3.15 StartZ=0 EndX=36.25 EndY=-7.15 EndZ=0
  constraints (16):
    c: Horizontal(g0)
    c: Distance(g0) = 2.7
    c: Horizontal(g1)
    c: Distance(g1) = 2.7
    c: Coincident(g1,g0)
    c: Block(g0)
    c: Coincident(g2,g0)
    c: Vertical(g2)
    c: Horizontal(g3)
    c: Coincident(g3,g2)
    c: Horizontal(g4)
    c: Coincident(g5,g1)
    c: Vertical(g5)
    c: Coincident(g5,g4)
    c: Block(g3)
    c: Block(g4)
FEATURE [Sketcher::SketchObject] Sketch024
  FullyConstrained = true
  Placement = pos=(0,-14.3,2.37) rot=(-1,0,0;2.03453rad)
  sketch-geometry (4):
    g0: LineSegment StartX=49.5 StartY=-21.2 StartZ=0 EndX=49.5 EndY=-22.8 EndZ=0
    g1: LineSegment StartX=49.5 StartY=-22.8 StartZ=0 EndX=0.002238 EndY=-22.8 EndZ=0
    g2: LineSegment StartX=0.002238 StartY=-21.2 StartZ=0 EndX=0.002238 EndY=-22.8 EndZ=0
    g3: LineSegment StartX=49.5 StartY=-21.2 StartZ=0 EndX=0.002238 EndY=-21.2 EndZ=0
  constraints (10):
    c: Vertical(g0)
    c: Distance(g0) = 1.6
    c: Coincident(g1,g0)
    c: Horizontal(g1)
    c: Vertical(g2)
    c: Coincident(g2,g1)
    c: Coincident(g3,g0)
    c: Coincident(g3,g2)
    c: Horizontal(g3)
    c: Block(g3)
FEATURE [Sketcher::SketchObject] Sketch025
  FullyConstrained = true
  Placement = pos=(0,-14.3,2.37) rot=(-1,0,0;2.03453rad)
  sketch-geometry (4):
    g0: LineSegment StartX=0 StartY=1.5 StartZ=0 EndX=0 EndY=0 EndZ=0
    g1: LineSegment StartX=0 StartY=1.5 StartZ=0 EndX=5 EndY=1.5 EndZ=0
    g2: LineSegment StartX=5 StartY=1.5 StartZ=0 EndX=5 EndY=0 EndZ=0
    g3: LineSegment StartX=0 StartY=0 StartZ=0 EndX=5 EndY=0 EndZ=0
  constraints (13):
    c: Vertical(g0)
    c: Distance(g0) = 1.5
    c: Horizontal(g1)
    c: Distance(g1) = 5
    c: Coincident(g1,g0)
    c: Vertical(g2)
    c: Distance(g2) = 1.5
    c: Coincident(g2,g1)
    c: Block(g1)
    c: Block(g2)
    c: Block(g0)
    c: Coincident(g3,g0)
    c: Coincident(g3,g2)
FEATURE [Part::Extrusion] Extrude022  label="solenoidDriverBottomLipTopExtrude014"
  Base = -> Sketch025
  Dir = (0,0.894389,-0.447291)
  DirMode = 2
  FaceMakerClass = Part::FaceMakerBullseye
  LengthFwd = -6.5
  LengthRev = 0
  Placement = pos=(0,-15.45,20.3) rot=(1,0,0;1.5708rad)
  Solid = true
  Symmetric = false
FEATURE [Part::Fillet] Fillet013  label="solenoidDriverBottomLipTopFillet006"
  Base = -> Extrude022
  Edges = 1 edges r=1.4: [Edge6]
  Placement = pos=(5,0,0) rot=(0,0,1;0rad)
FEATURE [Sketcher::SketchObject] Sketch026
  FullyConstrained = true
  Placement = pos=(0,-14.3,2.37) rot=(-1,0,0;2.03453rad)
  sketch-geometry (4):
    g0: LineSegment StartX=0 StartY=1.5 StartZ=0 EndX=0 EndY=0 EndZ=0
    g1: LineSegment StartX=0 StartY=1.5 StartZ=0 EndX=5 EndY=1.5 EndZ=0
    g2: LineSegment StartX=5 StartY=1.5 StartZ=0 EndX=5 EndY=0 EndZ=0
    g3: LineSegment StartX=0 StartY=0 StartZ=0 EndX=5 EndY=0 EndZ=0
  constraints (13):
    c: Vertical(g0)
    c: Distance(g0) = 1.5
    c: Horizontal(g1)
    c: Distance(g1) = 5
    c: Coincident(g1,g0)
    c: Vertical(g2)
    c: Distance(g2) = 1.5
    c: Coincident(g2,g1)
    c: Block(g1)
    c: Block(g2)
    c: Block(g0)
    c: Coincident(g3,g0)
    c: Coincident(g3,g2)
FEATURE [Part::Extrusion] Extrude023  label="solenoidDriverBottomLipTopExtrude015"
  Base = -> Sketch026
  Dir = (0,0.894389,-0.447291)
  DirMode = 2
  FaceMakerClass = Part::FaceMakerBullseye
  LengthFwd = -6.5
  LengthRev = 0
  Placement = pos=(5,-14.15,19.65) rot=(1,0,0;1.5708rad)
  Solid = true
  Symmetric = false
FEATURE [Sketcher::SketchObject] Sketch027
  FullyConstrained = true
  Placement = pos=(0,-14.3,2.37) rot=(-1,0,0;2.03453rad)
  sketch-geometry (5):
    g0: LineSegment StartX=45.5 StartY=-21.2 StartZ=0 EndX=49.5 EndY=-21.2 EndZ=0
    g1: LineSegment StartX=49.5 StartY=0 StartZ=0 EndX=49.5 EndY=-21.2 EndZ=0
    g2: LineSegment StartX=49.5 StartY=0 StartZ=0 EndX=49.5 EndY=1.6 EndZ=0
    g3: LineSegment StartX=45.5 StartY=-21.2 StartZ=0 EndX=45.5 EndY=1.6 EndZ=0
    g4: LineSegment StartX=49.5 StartY=1.6 StartZ=0 EndX=45.5 EndY=1.6 EndZ=0
  constraints (14):
    c: Horizontal(g0)
    c: Distance(g0) = 4
    c: Coincident(g1,g0)
    c: Vertical(g1)
    c: Block(g1)
    c: Vertical(g2)
    c: Distance(g2) = 1.6
    c: Block(g2)
    c: Coincident(g3,g0)
    c: Vertical(g3)
    c: Coincident(g4,g2)
    c: Horizontal(g4)
    c: Block(g0)
    c: Coincident(g3,g4)
FEATURE [Part::Extrusion] Extrude024
  Base = -> Sketch027
  Dir = (0,0.894389,-0.447291)
  DirMode = 2
  FaceMakerClass = Part::FaceMakerBullseye
  LengthFwd = 6.34
  LengthRev = 0
  Placement = pos=(0,-5.59,1) rot=(0,0,1;0rad)
  Solid = true
  Symmetric = false
FEATURE [Part::Fillet] Fillet014  label="solenoidDriverSideBarFillet014"
  Base = -> Extrude024
  Edges = 1 edges r=1.4: [Edge14]
  Placement = pos=(0,0.9,-0.45) rot=(0,0,1;0rad)
FEATURE [Part::Revolution] Revolve  label="mainScrewStandRevolve"
  Angle = 360
  Axis = (0,0,1)
  Base = (0,0,0)
  FaceMakerClass = Part::FaceMakerBullseye
  Placement = pos=(121.35,-15.3,0) rot=(0,0,1;0rad)
  Solid = true
  Source = -> Sketch004
  Symmetric = false
FEATURE [Part::Extrusion] Extrude021  label="solenoidDriverTopLipLowerExtrude011"
  Base = -> Sketch024
  Dir = (0,0.894389,-0.447291)
  DirMode = 2
  FaceMakerClass = Part::FaceMakerBullseye
  LengthFwd = 5.05
  LengthRev = 0
  Solid = true
  Symmetric = false
FEATURE [Part::Fillet] Fillet012  label="solenoidDriverTopLipLowerFillet004"
  Base = -> Extrude021
  Edges = 1 edges r=1.2: [Edge7]
  Placement = pos=(0,-0.9,-1.35) rot=(0,0,1;0rad)
FEATURE [Part::Fillet] Fillet003  label="solenoidDriverTopLipLowerFillet003"
  Base = -> Extrude010
  Edges = 1 edges r=1.2: [Edge7]
  Placement = pos=(0,-3,-0.3) rot=(0,0,1;0rad)
FEATURE [Part::Extrusion] Extrude025  label="mainBodyUpperExtrude025"
  Base = -> Sketch001
  Dir = (0,0,1)
  DirMode = 2
  FaceMakerClass = Part::FaceMakerBullseye
  LengthFwd = 20
  LengthRev = 0
  Solid = true
  Symmetric = false
FEATURE [Part::MultiFuse] Fusion  label="solenoidDriverBottomLipFusion"
  Placement = pos=(0,-1.6,0) rot=(0,0,1;0rad)
  Shapes = -> [Fillet005,Fillet013,Extrude023,Extrude013]
FEATURE [Sketcher::SketchObject] Sketch028
  FullyConstrained = true
  Placement = pos=(0,-14.3,2.37) rot=(-1,0,0;2.03453rad)
  sketch-geometry (4):
    g0: LineSegment StartX=0 StartY=1.5 StartZ=0 EndX=0 EndY=0 EndZ=0
    g1: LineSegment StartX=0 StartY=1.5 StartZ=0 EndX=5 EndY=1.5 EndZ=0
    g2: LineSegment StartX=5 StartY=1.5 StartZ=0 EndX=5 EndY=0 EndZ=0
    g3: LineSegment StartX=0 StartY=0 StartZ=0 EndX=5 EndY=0 EndZ=0
  constraints (13):
    c: Vertical(g0)
    c: Distance(g0) = 1.5
    c: Horizontal(g1)
    c: Distance(g1) = 5
    c: Coincident(g1,g0)
    c: Vertical(g2)
    c: Distance(g2) = 1.5
    c: Coincident(g2,g1)
    c: Block(g1)
    c: Block(g2)
    c: Block(g0)
    c: Coincident(g3,g0)
    c: Coincident(g3,g2)
FEATURE [Part::Extrusion] Extrude026  label="solenoidDriverBottomLipTopExtrude016"
  Base = -> Sketch028
  Dir = (0,0.894389,-0.447291)
  DirMode = 2
  FaceMakerClass = Part::FaceMakerBullseye
  LengthFwd = -6.5
  LengthRev = 0
  Placement = pos=(5,-14.15,19.65) rot=(1,0,0;1.5708rad)
  Solid = true
  Symmetric = false
FEATURE [Sketcher::SketchObject] Sketch029
  FullyConstrained = true
  Placement = pos=(0,-14.3,2.37) rot=(-1,0,0;2.03453rad)
  sketch-geometry (4):
    g0: LineSegment StartX=0 StartY=1.5 StartZ=0 EndX=0 EndY=0 EndZ=0
    g1: LineSegment StartX=0 StartY=1.5 StartZ=0 EndX=5 EndY=1.5 EndZ=0
    g2: LineSegment StartX=5 StartY=1.5 StartZ=0 EndX=5 EndY=0 EndZ=0
    g3: LineSegment StartX=0 StartY=0 StartZ=0 EndX=5 EndY=0 EndZ=0
  constraints (13):
    c: Vertical(g0)
    c: Distance(g0) = 1.5
    c: Horizontal(g1)
    c: Distance(g1) = 5
    c: Coincident(g1,g0)
    c: Vertical(g2)
    c: Distance(g2) = 1.5
    c: Coincident(g2,g1)
    c: Block(g1)
    c: Block(g2)
    c: Block(g0)
    c: Coincident(g3,g0)
    c: Coincident(g3,g2)
FEATURE [Part::Extrusion] Extrude027  label="solenoidDriverBottomLipTopExtrude017"
  Base = -> Sketch029
  Dir = (0,0.894389,-0.447291)
  DirMode = 2
  FaceMakerClass = Part::FaceMakerBullseye
  LengthFwd = -6.5
  LengthRev = 0
  Placement = pos=(0,-14.15,19.65) rot=(1,0,0;1.5708rad)
  Solid = true
  Symmetric = false
FEATURE [Sketcher::SketchObject] Sketch030
  FullyConstrained = true
  Placement = pos=(0,-14.3,2.37) rot=(-1,0,0;2.03453rad)
  sketch-geometry (4):
    g0: LineSegment StartX=0 StartY=1.5 StartZ=0 EndX=0 EndY=0 EndZ=0
    g1: LineSegment StartX=0 StartY=1.5 StartZ=0 EndX=5 EndY=1.5 EndZ=0
    g2: LineSegment StartX=5 StartY=1.5 StartZ=0 EndX=5 EndY=0 EndZ=0
    g3: LineSegment StartX=0 StartY=0 StartZ=0 EndX=5 EndY=0 EndZ=0
  constraints (13):
    c: Vertical(g0)
    c: Distance(g0) = 1.5
    c: Horizontal(g1)
    c: Distance(g1) = 5
    c: Coincident(g1,g0)
    c: Vertical(g2)
    c: Distance(g2) = 1.5
    c: Coincident(g2,g1)
    c: Block(g1)
    c: Block(g2)
    c: Block(g0)
    c: Coincident(g3,g0)
    c: Coincident(g3,g2)
FEATURE [Sketcher::SketchObject] Sketch031
  FullyConstrained = true
  Placement = pos=(0,-14.3,2.37) rot=(-1,0,0;2.03453rad)
  sketch-geometry (6):
    g0: LineSegment StartX=45.5 StartY=-21.2 StartZ=0 EndX=49.5 EndY=-21.2 EndZ=0
    g1: LineSegment StartX=45.5 StartY=0 StartZ=0 EndX=49.5 EndY=0 EndZ=0
    g2: LineSegment StartX=49.5 StartY=0 StartZ=0 EndX=49.5 EndY=-21.2 EndZ=0
    g3: LineSegment StartX=4 StartY=0 StartZ=0 EndX=4 EndY=-21.2 EndZ=0
    g4: LineSegment StartX=45.5 StartY=-21.2 StartZ=0 EndX=4 EndY=-21.2 EndZ=0
    g5: LineSegment StartX=4 StartY=0 StartZ=0 EndX=45.5 EndY=0 EndZ=0
  constraints (16):
    c: Horizontal(g0)
    c: Distance(g0) = 4
    c: Horizontal(g1)
    c: Distance(g1) = 4
    c: Coincident(g2,g1)
    c: Coincident(g2,g0)
    c: Vertical(g2)
    c: Block(g2)
    c: Vertical(g3)
    c: Coincident(g4,g0)
    c: Horizontal(g4)
    c: Coincident(g4,g3)
    c: Coincident(g5,g1)
    c: Horizontal(g5)
    c: Block(g3)
    c: Block(g5)
FEATURE [Part::Extrusion] Extrude028  label="removeFromSolenoidDriverMainExtrude021"
  Base = -> Sketch031
  Dir = (0,0.894389,-0.447291)
  DirMode = 2
  FaceMakerClass = Part::FaceMakerBullseye
  LengthFwd = 3.1
  LengthRev = 0
  Placement = pos=(-4,-2.42,-0.8) rot=(0,0,1;0rad)
  Solid = true
  Symmetric = false
FEATURE [Part::Extrusion] Extrude029  label="solenoidDriverBottomLipTopExtrude018"
  Base = -> Sketch030
  Dir = (0,0.894389,-0.447291)
  DirMode = 2
  FaceMakerClass = Part::FaceMakerBullseye
  LengthFwd = -6.5
  LengthRev = 0
  Placement = pos=(5,-14.15,19.65) rot=(1,0,0;1.5708rad)
  Solid = true
  Symmetric = false
FEATURE [Sketcher::SketchObject] Sketch032
  FullyConstrained = true
  Placement = pos=(0,-14.3,2.37) rot=(-1,0,0;2.03453rad)
  sketch-geometry (4):
    g0: LineSegment StartX=0 StartY=1.5 StartZ=0 EndX=0 EndY=0 EndZ=0
    g1: LineSegment StartX=0 StartY=1.5 StartZ=0 EndX=5 EndY=1.5 EndZ=0
    g2: LineSegment StartX=5 StartY=1.5 StartZ=0 EndX=5 EndY=0 EndZ=0
    g3: LineSegment StartX=0 StartY=0 StartZ=0 EndX=5 EndY=0 EndZ=0
  constraints (13):
    c: Vertical(g0)
    c: Distance(g0) = 1.5
    c: Horizontal(g1)
    c: Distance(g1) = 5
    c: Coincident(g1,g0)
    c: Vertical(g2)
    c: Distance(g2) = 1.5
    c: Coincident(g2,g1)
    c: Block(g1)
    c: Block(g2)
    c: Block(g0)
    c: Coincident(g3,g0)
    c: Coincident(g3,g2)
FEATURE [Part::Extrusion] Extrude030  label="solenoidDriverBottomLipTopExtrude019"
  Base = -> Sketch032
  Dir = (0,0.894389,-0.447291)
  DirMode = 2
  FaceMakerClass = Part::FaceMakerBullseye
  LengthFwd = -6.5
  LengthRev = 0
  Placement = pos=(0,-14.15,19.65) rot=(1,0,0;1.5708rad)
  Solid = true
  Symmetric = false
FEATURE [Part::MultiFuse] Fusion004
  Placement = pos=(0,1.4,2.65) rot=(0,0,1;0rad)
  Shapes = -> [Extrude029,Extrude030]
FEATURE [Part::MultiFuse] Fusion003
  Placement = pos=(-2.3,0,0) rot=(0,0,1;0rad)
  Shapes = -> [Extrude028,Fusion004]
FEATURE [Sketcher::SketchObject] Sketch033
  FullyConstrained = true
  Placement = pos=(0,-14.3,2.37) rot=(-1,0,0;2.03453rad)
  sketch-geometry (4):
    g0: LineSegment StartX=0 StartY=1.5 StartZ=0 EndX=0 EndY=0 EndZ=0
    g1: LineSegment StartX=0 StartY=1.5 StartZ=0 EndX=5 EndY=1.5 EndZ=0
    g2: LineSegment StartX=5 StartY=1.5 StartZ=0 EndX=5 EndY=0 EndZ=0
    g3: LineSegment StartX=0 StartY=0 StartZ=0 EndX=5 EndY=0 EndZ=0
  constraints (13):
    c: Vertical(g0)
    c: Distance(g0) = 1.5
    c: Horizontal(g1)
    c: Distance(g1) = 5
    c: Coincident(g1,g0)
    c: Vertical(g2)
    c: Distance(g2) = 1.5
    c: Coincident(g2,g1)
    c: Block(g1)
    c: Block(g2)
    c: Block(g0)
    c: Coincident(g3,g0)
    c: Coincident(g3,g2)
FEATURE [Sketcher::SketchObject] Sketch034
  FullyConstrained = true
  Placement = pos=(0,-14.3,2.37) rot=(-1,0,0;2.03453rad)
  sketch-geometry (4):
    g0: LineSegment StartX=0 StartY=1.5 StartZ=0 EndX=0 EndY=0 EndZ=0
    g1: LineSegment StartX=0 StartY=1.5 StartZ=0 EndX=5 EndY=1.5 EndZ=0
    g2: LineSegment StartX=5 StartY=1.5 StartZ=0 EndX=5 EndY=0 EndZ=0
    g3: LineSegment StartX=0 StartY=0 StartZ=0 EndX=5 EndY=0 EndZ=0
  constraints (13):
    c: Vertical(g0)
    c: Distance(g0) = 1.5
    c: Horizontal(g1)
    c: Distance(g1) = 5
    c: Coincident(g1,g0)
    c: Vertical(g2)
    c: Distance(g2) = 1.5
    c: Coincident(g2,g1)
    c: Block(g1)
    c: Block(g2)
    c: Block(g0)
    c: Coincident(g3,g0)
    c: Coincident(g3,g2)
FEATURE [Part::Extrusion] Extrude020  label="removeFromSolenoidDriverMainExtrude020"
  Base = -> Sketch020
  Dir = (0,0.894389,-0.447291)
  DirMode = 2
  FaceMakerClass = Part::FaceMakerBullseye
  LengthFwd = 3.1
  LengthRev = 0
  Placement = pos=(-4,-2.42,-0.8) rot=(0,0,1;0rad)
  Solid = true
  Symmetric = false
FEATURE [Part::Fillet] Fillet
  Base = -> Fusion003
  Edges = 1 edges r=10: [Edge5]
  Placement = pos=(-2,0,0) rot=(0,0,1;0rad)
FEATURE [Part::MultiFuse] Fusion001
  Placement = pos=(0,1.4,2.65) rot=(0,0,1;0rad)
  Shapes = -> [Extrude026,Extrude027]
FEATURE [Part::MultiFuse] Fusion002
  Shapes = -> [Extrude020,Fusion001]
FEATURE [Sketcher::SketchObject] Sketch035
  FullyConstrained = true
  Placement = pos=(0,-14.3,2.37) rot=(-1,0,0;2.03453rad)
  sketch-geometry (4):
    g0: LineSegment StartX=0 StartY=1.5 StartZ=0 EndX=0 EndY=0 EndZ=0
    g1: LineSegment StartX=0 StartY=1.5 StartZ=0 EndX=5 EndY=1.5 EndZ=0
    g2: LineSegment StartX=5 StartY=1.5 StartZ=0 EndX=5 EndY=0 EndZ=0
    g3: LineSegment StartX=0 StartY=0 StartZ=0 EndX=5 EndY=0 EndZ=0
  constraints (13):
    c: Vertical(g0)
    c: Distance(g0) = 1.5
    c: Horizontal(g1)
    c: Distance(g1) = 5
    c: Coincident(g1,g0)
    c: Vertical(g2)
    c: Distance(g2) = 1.5
    c: Coincident(g2,g1)
    c: Block(g1)
    c: Block(g2)
    c: Block(g0)
    c: Coincident(g3,g0)
    c: Coincident(g3,g2)
FEATURE [Sketcher::SketchObject] Sketch036
  FullyConstrained = true
  Placement = pos=(0,-14.3,2.37) rot=(-1,0,0;2.03453rad)
  sketch-geometry (4):
    g0: LineSegment StartX=0 StartY=1.5 StartZ=0 EndX=0 EndY=0 EndZ=0
    g1: LineSegment StartX=0 StartY=1.5 StartZ=0 EndX=5 EndY=1.5 EndZ=0
    g2: LineSegment StartX=5 StartY=1.5 StartZ=0 EndX=5 EndY=0 EndZ=0
    g3: LineSegment StartX=0 StartY=0 StartZ=0 EndX=5 EndY=0 EndZ=0
  constraints (13):
    c: Vertical(g0)
    c: Distance(g0) = 1.5
    c: Horizontal(g1)
    c: Distance(g1) = 5
    c: Coincident(g1,g0)
    c: Vertical(g2)
    c: Distance(g2) = 1.5
    c: Coincident(g2,g1)
    c: Block(g1)
    c: Block(g2)
    c: Block(g0)
    c: Coincident(g3,g0)
    c: Coincident(g3,g2)
FEATURE [Part::Extrusion] Extrude031  label="solenoidDriverBottomLipTopExtrude020"
  Base = -> Sketch035
  Dir = (0,0.894389,-0.447291)
  DirMode = 2
  FaceMakerClass = Part::FaceMakerBullseye
  LengthFwd = -6.5
  LengthRev = 0
  Placement = pos=(5,-14.15,19.65) rot=(1,0,0;1.5708rad)
  Solid = true
  Symmetric = false
FEATURE [Part::Extrusion] Extrude032  label="solenoidDriverBottomLipTopExtrude021"
  Base = -> Sketch036
  Dir = (0,0.894389,-0.447291)
  DirMode = 2
  FaceMakerClass = Part::FaceMakerBullseye
  LengthFwd = -6.5
  LengthRev = 0
  Placement = pos=(0,-14.15,19.65) rot=(1,0,0;1.5708rad)
  Solid = true
  Symmetric = false
FEATURE [Part::MultiFuse] Fusion009
  Placement = pos=(8,1.4,2.65) rot=(0,0,1;0rad)
  Shapes = -> [Extrude031,Extrude032]
FEATURE [Part::MultiFuse] Fusion010  label="removeFromSolenoidDriver"
  Shapes = -> [Fusion009,Fillet,Fusion002]
FEATURE [Sketcher::SketchObject] Sketch037
  FullyConstrained = true
  Placement = pos=(0,0,0) rot=(1,0,0;1.5708rad)
  sketch-geometry (4):
    g0: Circle CenterX=64.05 CenterY=16.5 CenterZ=0 NormalX=0 NormalY=0 NormalZ=1 AngleXU=0 Radius=2.7
    g1: Circle CenterX=64.05 CenterY=8.5 CenterZ=0 NormalX=0 NormalY=0 NormalZ=1 AngleXU=0 Radius=2.7
    g2: Circle CenterX=84.15 CenterY=8.5 CenterZ=0 NormalX=0 NormalY=0 NormalZ=1 AngleXU=0 Radius=2.7
    g3: Circle CenterX=84.15 CenterY=16.5 CenterZ=0 NormalX=0 NormalY=0 NormalZ=1 AngleXU=0 Radius=2.7
  constraints (4):
    c: Block(g2)
    c: Block(g3)
    c: Block(g0)
    c: Block(g1)
FEATURE [Part::Extrusion] Extrude033  label="removeFromMainBodyToCreateScrewHoleCounterSinks001"
  Base = -> Sketch037
  Dir = (0,-1,1.1e-15)
  DirMode = 2
  FaceMakerClass = Part::FaceMakerBullseye
  LengthFwd = 1.9
  LengthRev = 0
  Placement = pos=(0.8,0,0) rot=(0,0,1;0rad)
  Solid = true
  Symmetric = false
FEATURE [Part::MultiFuse] Fusion011  label="removeFromMainBodyToCreateScrewHoleCounterSinks001Fusion011"
  Shapes = -> [Extrude014,Extrude033]
FEATURE [Sketcher::SketchObject] Sketch038
  FullyConstrained = true
  Placement = pos=(0,-14.3,2.37) rot=(-1,0,0;2.03453rad)
  sketch-geometry (4):
    g0: LineSegment StartX=33.9 StartY=-9.7 StartZ=0 EndX=33.9 EndY=-1.5 EndZ=0
    g1: LineSegment StartX=33.9 StartY=-1.5 StartZ=0 EndX=44.5 EndY=-1.5 EndZ=0
    g2: LineSegment StartX=33.9 StartY=-9.7 StartZ=0 EndX=44.5 EndY=-9.7 EndZ=0
    g3: LineSegment StartX=44.5 StartY=-1.5 StartZ=0 EndX=44.5 EndY=-9.7 EndZ=0
  constraints (10):
    c: Vertical(g0)
    c: Coincident(g1,g0)
    c: Horizontal(g1)
    c: Block(g1)
    c: Block(g0)
    c: Coincident(g2,g0)
    c: Horizontal(g2)
    c: Coincident(g3,g1)
    c: Coincident(g3,g2)
    c: Vertical(g3)
FEATURE [Part::Extrusion] Extrude034
  Base = -> Sketch038
  Dir = (0,0.894389,-0.447291)
  DirMode = 2
  FaceMakerClass = Part::FaceMakerBullseye
  LengthFwd = 16
  LengthRev = 0
  Placement = pos=(0,-22,7) rot=(0,0,1;0rad)
  Solid = true
  Symmetric = false
FEATURE [Sketcher::SketchObject] Sketch039
  FullyConstrained = true
  Placement = pos=(0,-14.3,2.37) rot=(-1,0,0;2.03453rad)
  sketch-geometry (4):
    g0: LineSegment StartX=5.5 StartY=-7.7 StartZ=0 EndX=13.3 EndY=-7.7 EndZ=0
    g1: LineSegment StartX=13.3 StartY=-7.7 StartZ=0 EndX=13.3 EndY=-13.1 EndZ=0
    g2: LineSegment StartX=13.3 StartY=-13.1 StartZ=0 EndX=5.5 EndY=-13.1 EndZ=0
    g3: LineSegment StartX=5.5 StartY=-7.7 StartZ=0 EndX=5.5 EndY=-13.1 EndZ=0
  constraints (12):
    c: Horizontal(g0)
    c: Distance(g0) = 7.8
    c: Coincident(g1,g0)
    c: Vertical(g1)
    c: Distance(g1) = 5.4
    c: Coincident(g2,g1)
    c: Horizontal(g2)
    c: Vertical(g3)
    c: Coincident(g3,g2)
    c: Block(g0)
    c: Block(g2)
    c: Block(g3)
FEATURE [Part::Extrusion] Extrude035  label="removeToMakeHoleForConnectorExtrude035"
  Base = -> Sketch039
  Dir = (0,0.894389,-0.447291)
  DirMode = 2
  FaceMakerClass = Part::FaceMakerBullseye
  LengthFwd = 15
  LengthRev = 0
  Placement = pos=(-4,-22,9.6469) rot=(0,0,1;0rad)
  Solid = true
  Symmetric = false
FEATURE [App::MeasureDistance] Distance  label="Distance: 4.00 mm"
  Distance = 4.00184
  P1 = (119.349,-15.3,8)
  P2 = (123.351,-15.3,8)
FEATURE [App::MeasureDistance] Distance001  label="Distance: 3.80 mm"
  Distance = 3.8
  P1 = (119.45,-15.3,8)
  P2 = (123.25,-15.3,8)
FEATURE [Part::Fillet] Fillet015
  Base = -> Extrude009
  Edges = 1 edges r=1.59: [Edge7]
FEATURE [Part::Fillet] Fillet016
  Base = -> Extrude017
  Edges = 1 edges r=1.49: [Edge12]
FEATURE [Part::Fillet] Fillet017
  Base = -> Fillet016
  Edges = 1 edges r=1.45: [Edge8]
FEATURE [Part::MultiFuse] Fusion012  label="main"
  Shapes = -> [Extrude,Revolve,Extrude005,Fillet003,Fillet012,Fillet014,Extrude025,Fusion,Fillet015,Fillet017]
FEATURE [Part::Cut] Cut001
  Base = -> Fusion012
  Tool = -> Box003
FEATURE [Part::Cut] Cut002
  Base = -> Cut001
  Tool = -> Box002
FEATURE [Part::Cut] Cut003
  Base = -> Cut002
  Tool = -> Cut
FEATURE [Part::Cut] Cut004
  Base = -> Cut003
  Tool = -> Extrude019
FEATURE [Part::Cut] Cut005
  Base = -> Cut004
  Tool = -> Fusion011
FEATURE [Part::Cut] Cut006
  Base = -> Cut005
  Tool = -> Extrude004
FEATURE [Part::Cut] Cut007
  Base = -> Cut006
  Tool = -> Extrude015
FEATURE [Part::Cut] Cut008
  Base = -> Cut007
  Tool = -> Extrude008
FEATURE [Part::Cut] Cut009
  Base = -> Cut008
  Tool = -> Fusion010
FEATURE [App::MeasureDistance] Distance002  label="Distance: 2.05 mm"
  Distance = 2.05453
  P1 = (1.5,-23.0732,21.402)
  P2 = (6e-15,-23,20)
FEATURE [Part::Cut] Cut010
  Base = -> Cut009
  Tool = -> Extrude035
FEATURE [Part::Cut] Cut011
  Base = -> Cut010
  Tool = -> Extrude034
FEATURE [Part::Fillet] Fillet018
  Base = -> Cut011
  Edges = 1 edges r=3: [Edge134]
FEATURE [Part::Fillet] Fillet019
  Base = -> Fillet018
  Edges = 1 edges r=3: [Edge29]
FEATURE [Part::Box] Box004  label="Cube004"
  AttacherType = Attacher::AttachEngine3D
  Height = 10
  Length = 200
  Placement = pos=(-30,0,0) rot=(0,0,1;0rad)
  Width = 10
FEATURE [Part::Fillet] Fillet020
  Base = -> Box004
  Edges = 1 edges r=3.6: [Edge12]
FEATURE [Part::Box] Box005  label="Cube005"
  AttacherType = Attacher::AttachEngine3D
  Height = 10
  Length = 198
  Placement = pos=(-30,0,0) rot=(0,0,1;0rad)
  Width = 10
FEATURE [Part::Cut] Cut012
  Base = -> Box005
  Tool = -> Fillet020
FEATURE [Part::Box] Box006  label="Cube006"
  AttacherType = Attacher::AttachEngine3D
  Height = 5
  Length = 200
  Placement = pos=(-30,6.4,10) rot=(1,0,0;0rad)
  Width = 5
FEATURE [Part::Box] Box007  label="Cube007"
  AttacherType = Attacher::AttachEngine3D
  Height = 5
  Length = 200
  Placement = pos=(-30,6.4,10) rot=(1,0,0;0.872665rad)
  Width = 5
FEATURE [Part::MultiFuse] Fusion013  label="removeFromMainFusion013"
  Placement = pos=(0,-10,10) rot=(0,0,1;0rad)
  Shapes = -> [Box007,Box006,Cut012]
FEATURE [Part::Cut] Cut013
  Base = -> Fillet019
  Tool = -> Fusion013
FEATURE [Mesh::Feature] v0_98_Cut013  label="v0_98-Cut013"
FEATURE [App::MeasureDistance] Distance003  label="Distance: 7.18 mm"
  Distance = 7.17719
  P1 = (117.773,-15.3145,-2.4)
  P2 = (124.951,-15.2973,-2.4)
FEATURE [Sketcher::SketchObject] Sketch040
  FullyConstrained = true
  Placement = pos=(0,-14.3,2.37) rot=(-1,0,0;2.03453rad)
  sketch-geometry (4):
    g0: LineSegment StartX=0 StartY=1.5 StartZ=0 EndX=0 EndY=0 EndZ=0
    g1: LineSegment StartX=0 StartY=1.5 StartZ=0 EndX=5 EndY=1.5 EndZ=0
    g2: LineSegment StartX=5 StartY=1.5 StartZ=0 EndX=5 EndY=0 EndZ=0
    g3: LineSegment StartX=0 StartY=0 StartZ=0 EndX=5 EndY=0 EndZ=0
  constraints (13):
    c: Vertical(g0)
    c: Distance(g0) = 1.5
    c: Horizontal(g1)
    c: Distance(g1) = 5
    c: Coincident(g1,g0)
    c: Vertical(g2)
    c: Distance(g2) = 1.5
    c: Coincident(g2,g1)
    c: Block(g1)
    c: Block(g2)
    c: Block(g0)
    c: Coincident(g3,g0)
    c: Coincident(g3,g2)
FEATURE [Part::Extrusion] Extrude036
  Base = -> Sketch040
  Dir = (0,0.894389,-0.447291)
  DirMode = 2
  FaceMakerClass = Part::FaceMakerBullseye
  LengthFwd = 1.4
  LengthRev = 0
  Placement = pos=(0,8.25,17.58) rot=(0,0,1;0rad)
  Solid = true
  Symmetric = false
FEATURE [Sketcher::SketchObject] Sketch041
  FullyConstrained = true
  Placement = pos=(0,-14.3,2.37) rot=(-1,0,0;2.03453rad)
  sketch-geometry (4):
    g0: LineSegment StartX=0 StartY=1.5 StartZ=0 EndX=0 EndY=0 EndZ=0
    g1: LineSegment StartX=0 StartY=1.5 StartZ=0 EndX=5 EndY=1.5 EndZ=0
    g2: LineSegment StartX=5 StartY=1.5 StartZ=0 EndX=5 EndY=0 EndZ=0
    g3: LineSegment StartX=0 StartY=0 StartZ=0 EndX=5 EndY=0 EndZ=0
  constraints (13):
    c: Vertical(g0)
    c: Distance(g0) = 1.5
    c: Horizontal(g1)
    c: Distance(g1) = 5
    c: Coincident(g1,g0)
    c: Vertical(g2)
    c: Distance(g2) = 1.5
    c: Coincident(g2,g1)
    c: Block(g1)
    c: Block(g2)
    c: Block(g0)
    c: Coincident(g3,g0)
    c: Coincident(g3,g2)
FEATURE [Part::Extrusion] Extrude037
  Base = -> Sketch041
  Dir = (0,0.894389,-0.447291)
  DirMode = 2
  FaceMakerClass = Part::FaceMakerBullseye
  LengthFwd = 1.4
  LengthRev = 0
  Placement = pos=(0,6.11,13.33) rot=(0,0,1;0rad)
  Solid = true
  Symmetric = false
FEATURE [Part::MultiFuse] Fusion014  label="screwSpacerFusion014"
  Shapes = -> [Extrude037,Extrude036]
FEATURE [Sketcher::SketchObject] Sketch042
  FullyConstrained = true
  Placement = pos=(0,-14.3,2.37) rot=(-1,0,0;2.03453rad)
  sketch-geometry (4):
    g0: LineSegment StartX=0 StartY=1.5 StartZ=0 EndX=0 EndY=0 EndZ=0
    g1: LineSegment StartX=0 StartY=1.5 StartZ=0 EndX=5 EndY=1.5 EndZ=0
    g2: LineSegment StartX=5 StartY=1.5 StartZ=0 EndX=5 EndY=0 EndZ=0
    g3: LineSegment StartX=0 StartY=0 StartZ=0 EndX=5 EndY=0 EndZ=0
  constraints (13):
    c: Vertical(g0)
    c: Distance(g0) = 1.5
    c: Horizontal(g1)
    c: Distance(g1) = 5
    c: Coincident(g1,g0)
    c: Vertical(g2)
    c: Distance(g2) = 1.5
    c: Coincident(g2,g1)
    c: Block(g1)
    c: Block(g2)
    c: Block(g0)
    c: Coincident(g3,g0)
    c: Coincident(g3,g2)
FEATURE [Part::Extrusion] Extrude038
  Base = -> Sketch042
  Dir = (0,0.894389,-0.447291)
  DirMode = 2
  FaceMakerClass = Part::FaceMakerBullseye
  LengthFwd = 1.4
  LengthRev = 0
  Placement = pos=(0,8.459,18) rot=(0,0,1;0rad)
  Solid = true
  Symmetric = false
FEATURE [Part::MultiFuse] Fusion015  label="screwSpacerFusion014Fusion015"
  Placement = pos=(0,0.35,-0.18) rot=(0,0,1;0rad)
  Shapes = -> [Extrude038,Fusion014]
